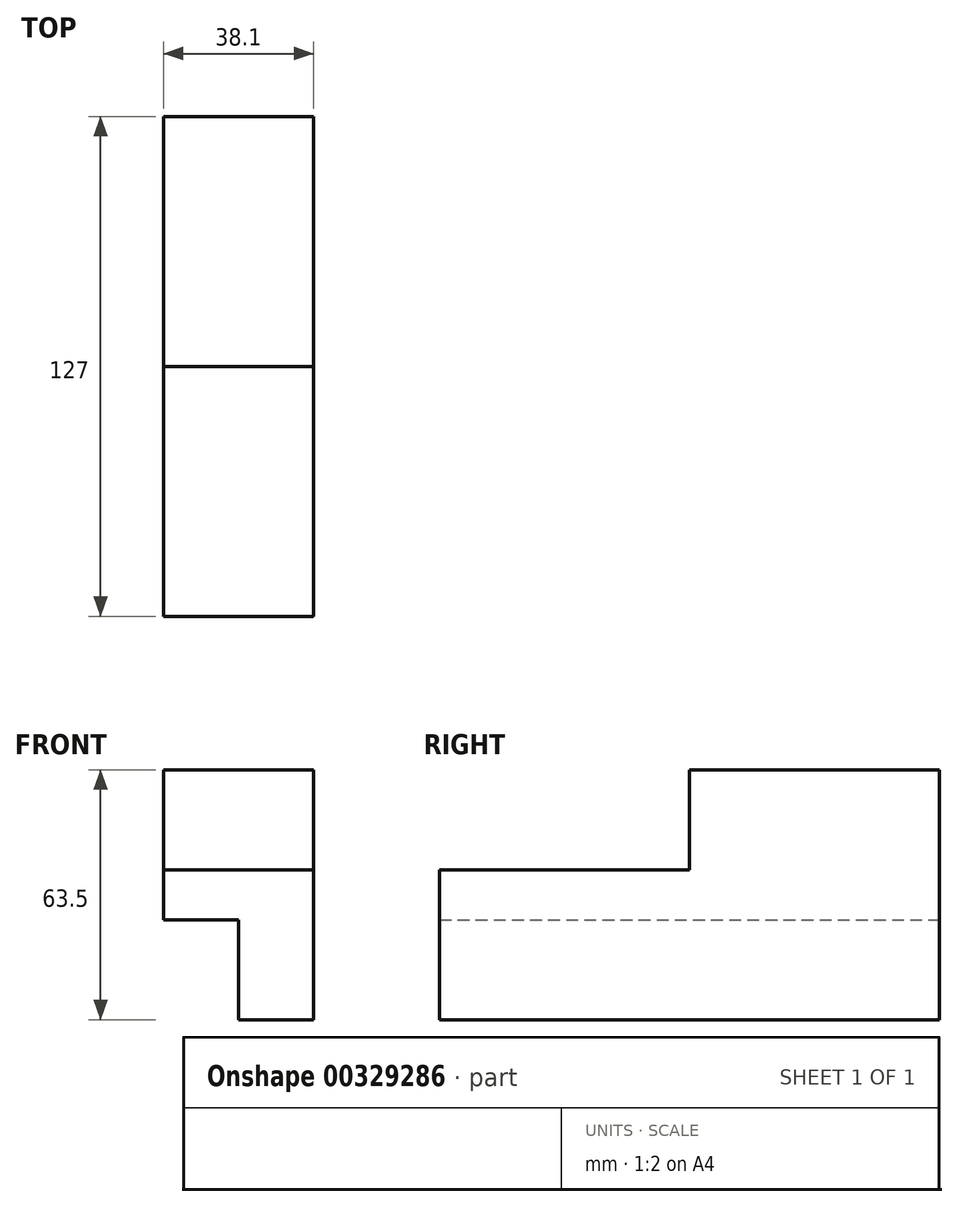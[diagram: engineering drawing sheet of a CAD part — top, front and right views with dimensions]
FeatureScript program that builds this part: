
annotation { "Feature Type Name" : "Feature", "Feature Type Description" : "" }
export const myFeature = defineFeature(function(context is Context, id is Id, definition is map)
    precondition{}
    {
        {
            var Q0;
            Q0=qCreatedBy(makeId("Front.planeOp"),FACE);
            var sketch = newSketch(context, id + "F0", { "sketchPlane" : qUnion([Q0])});
            skLineSegment(sketch, "E0", {"start": v(40.71, -38.1) * mm, "end": v(40.71, 25.4) * mm});
            skLineSegment(sketch, "E1", {"start": v(40.71, -38.1) * mm, "end": v(21.66, -38.1) * mm});
            skLineSegment(sketch, "E2", {"start": v(21.66, -38.1) * mm, "end": v(21.66, -12.7) * mm});
            skLineSegment(sketch, "E3", {"start": v(21.66, -12.7) * mm, "end": v(2.61, -12.7) * mm});
            skLineSegment(sketch, "E4", {"start": v(2.61, -12.7) * mm, "end": v(2.61, 0) * mm});
            skLineSegment(sketch, "E5", {"start": v(2.61, 0) * mm, "end": v(40.71, 0) * mm});
            skLineSegment(sketch, "E6", {"start": v(2.61, 0) * mm, "end": v(2.61, 25.4) * mm});
            skLineSegment(sketch, "E7", {"start": v(2.61, 25.4) * mm, "end": v(40.71, 25.4) * mm});
            skSolve(sketch);
        }
        {
            var Q0;
            {var subQ0=sQuery(id+"F0.wireOp",EDGE,"E1");Q0=makeQuery(id+"F0.imprint","IMPRINT",FACE,{"disambiguationData":[TD([[makeQuery(id+"F0.imprint","IMPRINT",EDGE,{"derivedFrom":subQ0}),-1.0]])]});}
            extrude(context, id + "F1", {"entities" : qUnion([Q0]), "depth" : 127 * mm});
        }
        {
            var Q0;
            Q0 = qSketchRegion(id + "F0", true);
            extrude(context, id + "F2", {"entities" : qUnion([Q0]), "operationType" : NewBodyOperationType.ADD, "depth" : 63.5 * mm});
        }
    });
